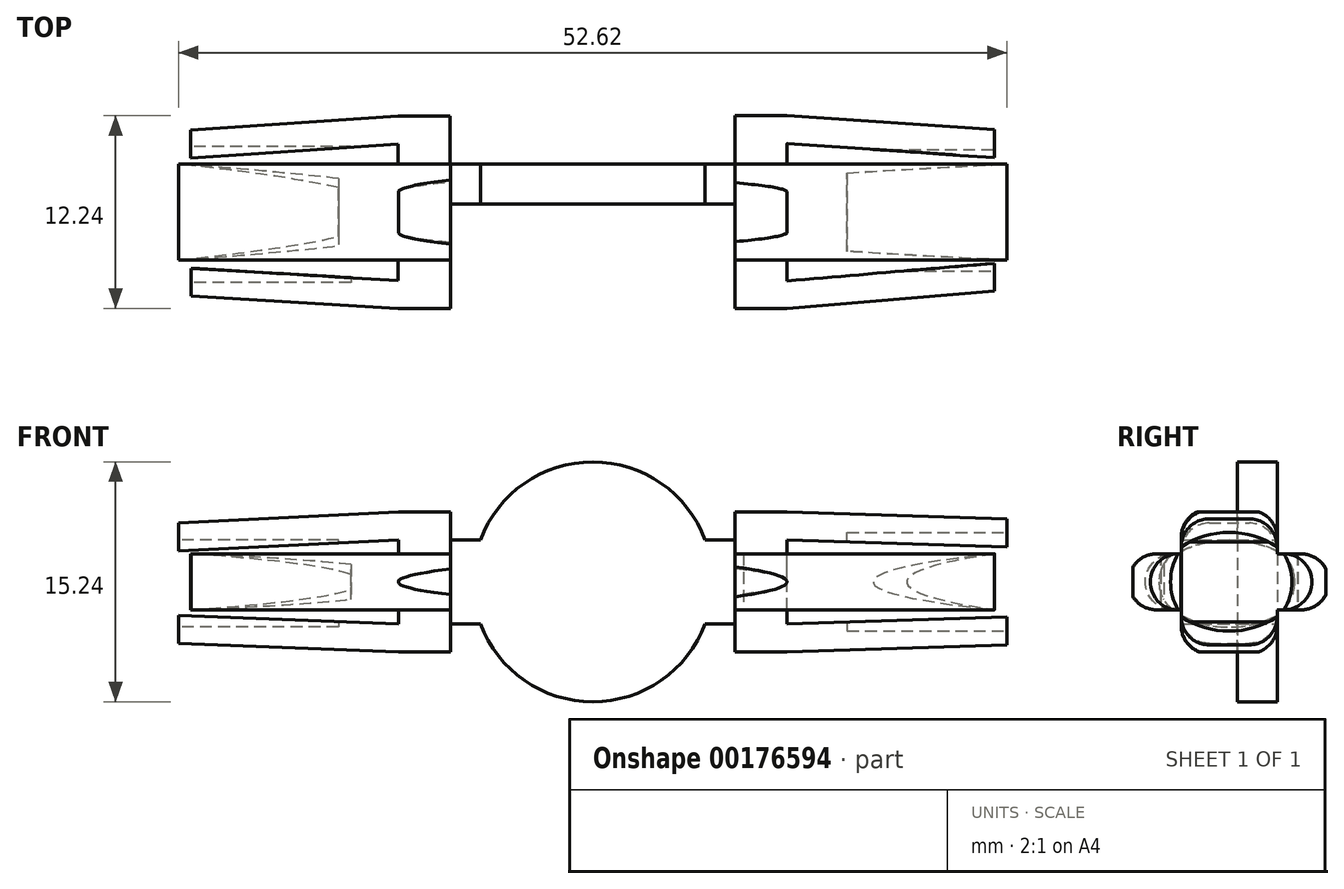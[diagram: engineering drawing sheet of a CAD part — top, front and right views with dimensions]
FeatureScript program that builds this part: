
annotation { "Feature Type Name" : "Feature", "Feature Type Description" : "" }
export const myFeature = defineFeature(function(context is Context, id is Id, definition is map)
    precondition{}
    {
        {
            var Q0;
            Q0=qCreatedBy(makeId("Front.planeOp"),FACE);
            var sketch = newSketch(context, id + "F0", { "sketchPlane" : qUnion([Q0])});
            skArc(sketch, "E0", {"start": v(7.14, 2.67) * mm, "mid": v(0, 7.62) * mm, "end": v(-7.14, 2.67) * mm});
            skLineSegment(sketch, "E1", {"start": v(-7.14, 2.67) * mm, "end": v(-9.04, 2.67) * mm});
            skLineSegment(sketch, "E2", {"start": v(-7.14, -2.67) * mm, "end": v(-9.04, -2.67) * mm});
            skLineSegment(sketch, "E3", {"start": v(-9.04, -2.67) * mm, "end": v(-9.04, 2.67) * mm});
            skLineSegment(sketch, "E4", {"start": v(7.14, 2.67) * mm, "end": v(9.04, 2.67) * mm});
            skLineSegment(sketch, "E5", {"start": v(7.14, -2.67) * mm, "end": v(9.04, -2.67) * mm});
            skLineSegment(sketch, "E6", {"start": v(9.04, -2.67) * mm, "end": v(9.04, 2.67) * mm});
            skArc(sketch, "E7.trimOffspring", {"start": v(-7.14, -2.67) * mm, "mid": v(0, -7.62) * mm, "end": v(7.14, -2.67) * mm});
            skLineSegment(sketch, "E8", {"start": v(-12.35, -2.67) * mm, "end": v(-12.35, 2.67) * mm});
            skLineSegment(sketch, "E9", {"start": v(-9.04, -2.67) * mm, "end": v(-9.04, -4.45) * mm});
            skLineSegment(sketch, "E10", {"start": v(-9.04, -4.45) * mm, "end": v(-12.35, -4.45) * mm});
            skLineSegment(sketch, "E11", {"start": v(-12.35, -4.45) * mm, "end": v(-26.3, -3.9) * mm});
            skLineSegment(sketch, "E12", {"start": v(-26.3, -3.9) * mm, "end": v(-26.3, -2.13) * mm});
            skLineSegment(sketch, "E13", {"start": v(-26.3, -2.13) * mm, "end": v(-12.35, -2.67) * mm});
            skLineSegment(sketch, "E14", {"start": v(-9.04, 2.67) * mm, "end": v(-9.04, 4.45) * mm});
            skLineSegment(sketch, "E15", {"start": v(-9.04, 4.45) * mm, "end": v(-12.35, 4.45) * mm});
            skLineSegment(sketch, "E16", {"start": v(-12.35, 4.45) * mm, "end": v(-26.3, 3.73) * mm});
            skLineSegment(sketch, "E17", {"start": v(-26.3, 3.73) * mm, "end": v(-26.3, 1.95) * mm});
            skLineSegment(sketch, "E18", {"start": v(-26.3, 1.95) * mm, "end": v(-12.35, 2.67) * mm});
            skLineSegment(sketch, "E19", {"start": v(9.04, 2.67) * mm, "end": v(9.04, 4.44) * mm});
            skLineSegment(sketch, "E20", {"start": v(9.04, 4.44) * mm, "end": v(12.35, 4.44) * mm});
            skLineSegment(sketch, "E21", {"start": v(9.04, -2.67) * mm, "end": v(9.04, -4.44) * mm});
            skLineSegment(sketch, "E22", {"start": v(9.04, -4.44) * mm, "end": v(12.35, -4.44) * mm});
            skLineSegment(sketch, "E23", {"start": v(12.35, -2.67) * mm, "end": v(12.35, 2.67) * mm});
            skLineSegment(sketch, "E24", {"start": v(12.35, -4.44) * mm, "end": v(26.3, -4) * mm});
            skLineSegment(sketch, "E25", {"start": v(26.3, -4) * mm, "end": v(26.3, -2.23) * mm});
            skLineSegment(sketch, "E26", {"start": v(26.3, -2.23) * mm, "end": v(12.35, -2.67) * mm});
            skLineSegment(sketch, "E27", {"start": v(12.35, 4.44) * mm, "end": v(26.3, 4) * mm});
            skLineSegment(sketch, "E28", {"start": v(26.3, 4) * mm, "end": v(26.3, 2.23) * mm});
            skLineSegment(sketch, "E29", {"start": v(26.3, 2.23) * mm, "end": v(12.35, 2.67) * mm});
            skLineSegment(sketch, "E30", {"start": v(12.35, 4.44) * mm, "end": v(12.35, 2.67) * mm});
            skLineSegment(sketch, "E31", {"start": v(12.35, -4.44) * mm, "end": v(12.35, -2.67) * mm});
            skSolve(sketch);
        }
        {
            var Q0;
            Q0 = qSketchRegion(id + "F0", true);
            extrude(context, id + "F1", {"entities" : qUnion([Q0]), "depth" : 6.1 * mm});
        }
        {
            var Q0;
            Q0=makeQuery(id+"F1.opExtrude","CAP_FACE",FACE,{"disambiguationData":[OSD([sQuery(id+"F0.wireOp",EDGE,"E0"),sQuery(id+"F0.wireOp",EDGE,"E1"),sQuery(id+"F0.wireOp",EDGE,"E2"),sQuery(id+"F0.wireOp",EDGE,"E4"),sQuery(id+"F0.wireOp",EDGE,"E5"),sQuery(id+"F0.wireOp",EDGE,"E7.trimOffspring"),sQuery(id+"F0.wireOp",EDGE,"E8"),sQuery(id+"F0.wireOp",EDGE,"E9"),sQuery(id+"F0.wireOp",EDGE,"E10"),sQuery(id+"F0.wireOp",EDGE,"E11"),sQuery(id+"F0.wireOp",EDGE,"E12"),sQuery(id+"F0.wireOp",EDGE,"E13"),sQuery(id+"F0.wireOp",EDGE,"E14"),sQuery(id+"F0.wireOp",EDGE,"E15"),sQuery(id+"F0.wireOp",EDGE,"E16"),sQuery(id+"F0.wireOp",EDGE,"E17"),sQuery(id+"F0.wireOp",EDGE,"E18"),sQuery(id+"F0.wireOp",EDGE,"E19"),sQuery(id+"F0.wireOp",EDGE,"E20"),sQuery(id+"F0.wireOp",EDGE,"E21"),sQuery(id+"F0.wireOp",EDGE,"E22"),sQuery(id+"F0.wireOp",EDGE,"E23"),sQuery(id+"F0.wireOp",EDGE,"E24"),sQuery(id+"F0.wireOp",EDGE,"E25"),sQuery(id+"F0.wireOp",EDGE,"E26"),sQuery(id+"F0.wireOp",EDGE,"E27"),sQuery(id+"F0.wireOp",EDGE,"E28"),sQuery(id+"F0.wireOp",EDGE,"E29")])],"isStart":false});
            var sketch = newSketch(context, id + "F2", { "sketchPlane" : qUnion([Q0])});
            skLineSegment(sketch, "E32", {"start": v(-9.04, 2.67) * mm, "end": v(-9.04, -2.67) * mm});
            skLineSegment(sketch, "E33", {"start": v(9.04, 2.67) * mm, "end": v(9.04, -2.67) * mm});
            skSolve(sketch);
        }
        {
            var Q0;
            Q0 = qSketchRegion(id + "F2", true);
            var Q1;
            Q1=makeQuery(id+"F2.imprint","IMPRINT",FACE,{"disambiguationData":[TD([[makeQuery(id+"F2.imprint","IMPRINT",EDGE,{"derivedFrom":sQuery(id+"F2.wireOp",EDGE,"E32")}),1.0]])]});
            extrude(context, id + "F3", {"entities" : qUnion([Q0, Q1]), "operationType" : NewBodyOperationType.REMOVE, "oppositeDirection" : true, "depth" : 3.56 * mm});
        }
        {
            var Q0;
            Q0=qCreatedBy(makeId("Top.planeOp"),FACE);
            var sketch = newSketch(context, id + "F4", { "sketchPlane" : qUnion([Q0])});
            skLineSegment(sketch, "E34", {"start": v(-9.05, 0) * mm, "end": v(-9.05, 3.06) * mm});
            skLineSegment(sketch, "E35", {"start": v(-12.36, 3.06) * mm, "end": v(-9.05, 3.06) * mm});
            skPoint(sketch, "E36.start.orphan", {"position": v(-12.36, 0) * mm});
            skLineSegment(sketch, "E37", {"start": v(-12.36, 3.06) * mm, "end": v(-25.54, 2.17) * mm});
            skLineSegment(sketch, "E38", {"start": v(-25.54, 2.17) * mm, "end": v(-25.54, 0.4) * mm});
            skLineSegment(sketch, "E39", {"start": v(-12.36, 1.27) * mm, "end": v(-25.54, 0.4) * mm});
            skLineSegment(sketch, "E40", {"start": v(-12.36, 1.27) * mm, "end": v(-12.36, 0) * mm});
            skLineSegment(sketch, "E41", {"start": v(-12.36, 0) * mm, "end": v(-9.05, 0) * mm});
            skSolve(sketch);
        }
        {
            var Q0;
            Q0 = qSketchRegion(id + "F4", true);
            extrude(context, id + "F5", {"entities" : qUnion([Q0]), "operationType" : NewBodyOperationType.ADD, "depth" : 1.78 * mm});
        }
        {
            var Q0;
            Q0=makeQuery(id+"F5.opExtrude","CAP_FACE",FACE,{"disambiguationData":[OSD([sQuery(id+"F4.wireOp",EDGE,"E34"),sQuery(id+"F4.wireOp",EDGE,"E35"),sQuery(id+"F4.wireOp",EDGE,"E37"),sQuery(id+"F4.wireOp",EDGE,"E38"),sQuery(id+"F4.wireOp",EDGE,"E39"),sQuery(id+"F4.wireOp",EDGE,"E40"),sQuery(id+"F4.wireOp",EDGE,"E41")])],"isStart":true});
            extrude(context, id + "F6", {"entities" : qUnion([Q0]), "operationType" : NewBodyOperationType.ADD, "depth" : 1.78 * mm});
        }
        {
            var Q0;
            Q0=qCreatedBy(makeId("Top.planeOp"),FACE);
            var sketch = newSketch(context, id + "F7", { "sketchPlane" : qUnion([Q0])});
            skLineSegment(sketch, "E42", {"start": v(-9.04, -6.1) * mm, "end": v(-9.04, -9.16) * mm});
            skLineSegment(sketch, "E43", {"start": v(-9.04, -9.16) * mm, "end": v(-12.35, -9.16) * mm});
            skLineSegment(sketch, "E44", {"start": v(-12.35, -7.39) * mm, "end": v(-12.35, -6.1) * mm});
            skLineSegment(sketch, "E45", {"start": v(-12.35, -6.1) * mm, "end": v(-9.04, -6.1) * mm});
            skLineSegment(sketch, "E46", {"start": v(-12.35, -9.16) * mm, "end": v(-25.52, -8.38) * mm});
            skLineSegment(sketch, "E47", {"start": v(-25.52, -8.38) * mm, "end": v(-25.52, -6.61) * mm});
            skLineSegment(sketch, "E48", {"start": v(-12.35, -7.39) * mm, "end": v(-25.52, -6.61) * mm});
            skSolve(sketch);
        }
        {
            var Q0;
            Q0=makeQuery(id+"F7.imprint","IMPRINT",FACE,{"disambiguationData":[TD([[makeQuery(id+"F7.imprint","IMPRINT",EDGE,{"derivedFrom":sQuery(id+"F7.wireOp",EDGE,"E42")}),-1.0]])]});
            extrude(context, id + "F8", {"entities" : qUnion([Q0]), "operationType" : NewBodyOperationType.ADD, "depth" : 1.78 * mm});
        }
        {
            var Q0;
            Q0=makeQuery(id+"F8.opExtrude","CAP_FACE",FACE,{"disambiguationData":[OSD([sQuery(id+"F7.wireOp",EDGE,"E42"),sQuery(id+"F7.wireOp",EDGE,"E43"),sQuery(id+"F7.wireOp",EDGE,"E44"),sQuery(id+"F7.wireOp",EDGE,"E45"),sQuery(id+"F7.wireOp",EDGE,"E46"),sQuery(id+"F7.wireOp",EDGE,"E47"),sQuery(id+"F7.wireOp",EDGE,"E48")])],"isStart":true});
            extrude(context, id + "F9", {"entities" : qUnion([Q0]), "operationType" : NewBodyOperationType.ADD, "depth" : 1.78 * mm});
        }
        {
            var Q0;
            {var subQ0=sQuery(id+"F7.wireOp",EDGE,"E47");Q0=makeQuery(id+"F9.boolean.opBoolean","MERGE",FACE,{"derivedFrom":[makeQuery(id+"F8.opExtrude","SWEPT_FACE",FACE,{"disambiguationData":[OSD([subQ0])]}),makeQuery(id+"F9.opExtrude","SWEPT_FACE",FACE,{"disambiguationData":[OSD([subQ0])]})]});}
            var sketch = newSketch(context, id + "F10", { "sketchPlane" : qUnion([Q0])});
            skArc(sketch, "E49", {"start": v(6.61, -1.78) * mm, "mid": v(7.5, 0) * mm, "end": v(6.61, 1.78) * mm});
            skLineSegment(sketch, "E50", {"start": v(6.61, 1.78) * mm, "end": v(6.61, -1.78) * mm});
            skSolve(sketch);
        }
        {
            var Q0;
            Q0 = qSketchRegion(id + "F10", true);
            extrude(context, id + "F11", {"entities" : qUnion([Q0]), "operationType" : NewBodyOperationType.REMOVE, "oppositeDirection" : true, "depth" : 10.16 * mm});
        }
        {
            var Q0;
            Q0=makeQuery(id+"F1.opExtrude","SWEPT_FACE",FACE,{"disambiguationData":[OSD([sQuery(id+"F0.wireOp",EDGE,"E17")])]});
            var sketch = newSketch(context, id + "F12", { "sketchPlane" : qUnion([Q0])});
            skArc(sketch, "E51", {"start": v(6.1, 1.95) * mm, "mid": v(3.05, 2.65) * mm, "end": v(0, 1.95) * mm});
            skLineSegment(sketch, "E52", {"start": v(6.1, 1.95) * mm, "end": v(0, 1.95) * mm});
            skSolve(sketch);
        }
        {
            var Q0;
            Q0 = qSketchRegion(id + "F12", true);
            extrude(context, id + "F13", {"entities" : qUnion([Q0]), "operationType" : NewBodyOperationType.REMOVE, "oppositeDirection" : true, "depth" : 10.16 * mm});
        }
        {
            var Q0;
            Q0=makeQuery(id+"F1.opExtrude","SWEPT_FACE",FACE,{"disambiguationData":[OSD([sQuery(id+"F0.wireOp",EDGE,"E12")])]});
            var sketch = newSketch(context, id + "F14", { "sketchPlane" : qUnion([Q0])});
            skArc(sketch, "E53", {"start": v(0, -2.13) * mm, "mid": v(3.05, -2.88) * mm, "end": v(6.1, -2.13) * mm});
            skLineSegment(sketch, "E54", {"start": v(6.1, -2.13) * mm, "end": v(0, -2.13) * mm});
            skSolve(sketch);
        }
        {
            var Q0;
            Q0 = qSketchRegion(id + "F14", true);
            extrude(context, id + "F15", {"entities" : qUnion([Q0]), "operationType" : NewBodyOperationType.REMOVE, "oppositeDirection" : true, "depth" : 10.16 * mm});
        }
        {
            var Q0;
            {var subQ0=sQuery(id+"F4.wireOp",EDGE,"E38");Q0=makeQuery(id+"F6.boolean.opBoolean","MERGE",FACE,{"derivedFrom":[makeQuery(id+"F5.opExtrude","SWEPT_FACE",FACE,{"disambiguationData":[OSD([subQ0])]}),makeQuery(id+"F6.opExtrude","SWEPT_FACE",FACE,{"disambiguationData":[OSD([subQ0])]})]});}
            var sketch = newSketch(context, id + "F16", { "sketchPlane" : qUnion([Q0])});
            skArc(sketch, "E55", {"start": v(-0.4, 1.78) * mm, "mid": v(-1.12, 0) * mm, "end": v(-0.4, -1.78) * mm});
            skLineSegment(sketch, "E56", {"start": v(-0.4, 1.78) * mm, "end": v(-0.4, -1.78) * mm});
            skSolve(sketch);
        }
        {
            var Q0;
            Q0 = qSketchRegion(id + "F16", true);
            extrude(context, id + "F17", {"entities" : qUnion([Q0]), "operationType" : NewBodyOperationType.REMOVE, "oppositeDirection" : true, "depth" : 10.16 * mm});
        }
        {
            var Q0;
            Q0=qCreatedBy(makeId("Top.planeOp"),FACE);
            var sketch = newSketch(context, id + "F18", { "sketchPlane" : qUnion([Q0])});
            skLineSegment(sketch, "E57", {"start": v(9.04, 0) * mm, "end": v(9.04, 3.08) * mm});
            skLineSegment(sketch, "E58", {"start": v(9.04, 3.08) * mm, "end": v(12.34, 3.08) * mm});
            skLineSegment(sketch, "E59", {"start": v(12.34, 0) * mm, "end": v(9.04, 0) * mm});
            skLineSegment(sketch, "E60", {"start": v(12.34, 3.08) * mm, "end": v(25.52, 2.2) * mm});
            skLineSegment(sketch, "E61", {"start": v(25.52, 2.2) * mm, "end": v(25.52, 0.41) * mm});
            skLineSegment(sketch, "E62", {"start": v(25.52, 0.41) * mm, "end": v(12.34, 1.31) * mm});
            skLineSegment(sketch, "E63.trimOffspring", {"start": v(12.34, 1.31) * mm, "end": v(12.34, 0) * mm});
            skSolve(sketch);
        }
        {
            var Q0;
            Q0 = qSketchRegion(id + "F18", true);
            extrude(context, id + "F19", {"entities" : qUnion([Q0]), "operationType" : NewBodyOperationType.ADD, "depth" : 1.78 * mm});
        }
        {
            var Q0;
            Q0=qCreatedBy(makeId("Top.planeOp"),FACE);
            var sketch = newSketch(context, id + "F20", { "sketchPlane" : qUnion([Q0])});
            skLineSegment(sketch, "E64", {"start": v(9.04, -6.1) * mm, "end": v(9.04, -9.16) * mm});
            skLineSegment(sketch, "E65", {"start": v(9.04, -9.16) * mm, "end": v(12.33, -9.16) * mm});
            skLineSegment(sketch, "E66", {"start": v(12.33, -7.41) * mm, "end": v(12.33, -6.1) * mm});
            skLineSegment(sketch, "E67", {"start": v(12.33, -6.1) * mm, "end": v(9.04, -6.1) * mm});
            skLineSegment(sketch, "E68", {"start": v(12.33, -9.16) * mm, "end": v(25.5, -8.07) * mm});
            skLineSegment(sketch, "E69", {"start": v(25.5, -8.07) * mm, "end": v(25.5, -6.3) * mm});
            skLineSegment(sketch, "E70", {"start": v(25.5, -6.3) * mm, "end": v(12.33, -7.41) * mm});
            skSolve(sketch);
        }
        {
            var Q0;
            Q0 = qSketchRegion(id + "F20", true);
            extrude(context, id + "F21", {"entities" : qUnion([Q0]), "operationType" : NewBodyOperationType.ADD, "depth" : 1.78 * mm});
        }
        {
            var Q0;
            Q0=makeQuery(id+"F21.opExtrude","CAP_FACE",FACE,{"disambiguationData":[OSD([sQuery(id+"F20.wireOp",EDGE,"E64"),sQuery(id+"F20.wireOp",EDGE,"E65"),sQuery(id+"F20.wireOp",EDGE,"E66"),sQuery(id+"F20.wireOp",EDGE,"E67"),sQuery(id+"F20.wireOp",EDGE,"E68"),sQuery(id+"F20.wireOp",EDGE,"E69"),sQuery(id+"F20.wireOp",EDGE,"E70")])],"isStart":true});
            extrude(context, id + "F22", {"entities" : qUnion([Q0]), "operationType" : NewBodyOperationType.ADD, "depth" : 1.78 * mm});
        }
        {
            var Q0;
            Q0=makeQuery(id+"F19.opExtrude","CAP_FACE",FACE,{"disambiguationData":[OSD([sQuery(id+"F18.wireOp",EDGE,"E57"),sQuery(id+"F18.wireOp",EDGE,"E58"),sQuery(id+"F18.wireOp",EDGE,"E59"),sQuery(id+"F18.wireOp",EDGE,"E60"),sQuery(id+"F18.wireOp",EDGE,"E61"),sQuery(id+"F18.wireOp",EDGE,"E62"),sQuery(id+"F18.wireOp",EDGE,"E63.trimOffspring")])],"isStart":true});
            extrude(context, id + "F23", {"entities" : qUnion([Q0]), "operationType" : NewBodyOperationType.ADD, "depth" : 1.78 * mm});
        }
        {
            var Q0;
            {var subQ0=sQuery(id+"F20.wireOp",EDGE,"E69");Q0=makeQuery(id+"F22.boolean.opBoolean","MERGE",FACE,{"derivedFrom":[makeQuery(id+"F21.opExtrude","SWEPT_FACE",FACE,{"disambiguationData":[OSD([subQ0])]}),makeQuery(id+"F22.opExtrude","SWEPT_FACE",FACE,{"disambiguationData":[OSD([subQ0])]})]});}
            var sketch = newSketch(context, id + "F24", { "sketchPlane" : qUnion([Q0])});
            skArc(sketch, "E71", {"start": v(-6.3, 1.78) * mm, "mid": v(-6.77, 0) * mm, "end": v(-6.3, -1.78) * mm});
            skLineSegment(sketch, "E72", {"start": v(-6.3, -1.78) * mm, "end": v(-6.3, 1.78) * mm});
            skSolve(sketch);
        }
        {
            var Q0;
            Q0=makeQuery(id+"F1.opExtrude","SWEPT_FACE",FACE,{"disambiguationData":[OSD([sQuery(id+"F0.wireOp",EDGE,"E25")])]});
            var sketch = newSketch(context, id + "F25", { "sketchPlane" : qUnion([Q0])});
            skArc(sketch, "E73", {"start": v(-6.1, -2.23) * mm, "mid": v(-3.05, -3.13) * mm, "end": v(0, -2.23) * mm});
            skLineSegment(sketch, "E74", {"start": v(-6.1, -2.23) * mm, "end": v(0, -2.23) * mm});
            skSolve(sketch);
        }
        {
            var Q0;
            {var subQ0=sQuery(id+"F18.wireOp",EDGE,"E61");Q0=makeQuery(id+"F23.boolean.opBoolean","MERGE",FACE,{"derivedFrom":[makeQuery(id+"F19.opExtrude","SWEPT_FACE",FACE,{"disambiguationData":[OSD([subQ0])]}),makeQuery(id+"F23.opExtrude","SWEPT_FACE",FACE,{"disambiguationData":[OSD([subQ0])]})]});}
            var sketch = newSketch(context, id + "F26", { "sketchPlane" : qUnion([Q0])});
            skArc(sketch, "E75", {"start": v(0.41, -1.78) * mm, "mid": v(0.94, 0) * mm, "end": v(0.41, 1.78) * mm});
            skLineSegment(sketch, "E76", {"start": v(0.41, -1.78) * mm, "end": v(0.41, 1.78) * mm});
            skSolve(sketch);
        }
        {
            var Q0;
            Q0=makeQuery(id+"F1.opExtrude","SWEPT_FACE",FACE,{"disambiguationData":[OSD([sQuery(id+"F0.wireOp",EDGE,"E28")])]});
            var sketch = newSketch(context, id + "F27", { "sketchPlane" : qUnion([Q0])});
            skArc(sketch, "E77", {"start": v(0, 2.23) * mm, "mid": v(-3.05, 3.14) * mm, "end": v(-6.1, 2.23) * mm});
            skLineSegment(sketch, "E78", {"start": v(-6.1, 2.23) * mm, "end": v(0, 2.23) * mm});
            skSolve(sketch);
        }
        {
            var Q0;
            Q0=makeQuery(id+"F24.imprint","IMPRINT",FACE,{"disambiguationData":[TD([[makeQuery(id+"F24.imprint","IMPRINT",EDGE,{"derivedFrom":sQuery(id+"F24.wireOp",EDGE,"E71")}),1.0]])]});
            var Q1;
            Q1=makeQuery(id+"F27.imprint","IMPRINT",FACE,{"disambiguationData":[TD([[makeQuery(id+"F27.imprint","IMPRINT",EDGE,{"derivedFrom":sQuery(id+"F27.wireOp",EDGE,"E77")}),1.0]])]});
            var Q2;
            Q2=makeQuery(id+"F26.imprint","IMPRINT",FACE,{"disambiguationData":[TD([[makeQuery(id+"F26.imprint","IMPRINT",EDGE,{"derivedFrom":sQuery(id+"F26.wireOp",EDGE,"E75")}),1.0]])]});
            var Q3;
            Q3=makeQuery(id+"F25.imprint","IMPRINT",FACE,{"disambiguationData":[TD([[makeQuery(id+"F25.imprint","IMPRINT",EDGE,{"derivedFrom":sQuery(id+"F25.wireOp",EDGE,"E73")}),1.0]])]});
            extrude(context, id + "F28", {"entities" : qUnion([Q0, Q1, Q2, Q3]), "operationType" : NewBodyOperationType.REMOVE, "oppositeDirection" : true, "depth" : 10.16 * mm});
        }
        {
            var Q0;
            Q0=makeQuery(id+"F22.opExtrude","CAP_EDGE",EDGE,{"disambiguationData":[OSD([sQuery(id+"F20.wireOp",EDGE,"E68")])],"isStart":false});
            var Q1;
            Q1=makeQuery(id+"F21.opExtrude","CAP_EDGE",EDGE,{"disambiguationData":[OSD([sQuery(id+"F20.wireOp",EDGE,"E68")])],"isStart":false});
            var Q2;
            Q2=makeQuery(id+"F1.opExtrude","CAP_EDGE",EDGE,{"disambiguationData":[OSD([sQuery(id+"F0.wireOp",EDGE,"E24")])],"isStart":false});
            var Q3;
            Q3=makeQuery(id+"F1.opExtrude","CAP_EDGE",EDGE,{"disambiguationData":[OSD([sQuery(id+"F0.wireOp",EDGE,"E24")])],"isStart":true});
            var Q4;
            Q4=makeQuery(id+"F1.opExtrude","CAP_EDGE",EDGE,{"disambiguationData":[OSD([sQuery(id+"F0.wireOp",EDGE,"E27")])],"isStart":false});
            var Q5;
            Q5=makeQuery(id+"F1.opExtrude","CAP_EDGE",EDGE,{"disambiguationData":[OSD([sQuery(id+"F0.wireOp",EDGE,"E27")])],"isStart":true});
            var Q6;
            Q6=makeQuery(id+"F23.opExtrude","CAP_EDGE",EDGE,{"disambiguationData":[OSD([sQuery(id+"F18.wireOp",EDGE,"E60")])],"isStart":false});
            var Q7;
            Q7=makeQuery(id+"F19.opExtrude","CAP_EDGE",EDGE,{"disambiguationData":[OSD([sQuery(id+"F18.wireOp",EDGE,"E60")])],"isStart":false});
            fillet(context, id + "F29", {"entities" : qUnion([Q0, Q1, Q2, Q3, Q4, Q5, Q6, Q7]), "radius" : 1.78 * mm, "tangentPropagation" : true, "allowEdgeOverflow" : false});
        }
        {
            var Q0;
            Q0=makeQuery(id+"F8.opExtrude","CAP_EDGE",EDGE,{"disambiguationData":[OSD([sQuery(id+"F7.wireOp",EDGE,"E46")])],"isStart":false});
            var Q1;
            Q1=makeQuery(id+"F9.opExtrude","CAP_EDGE",EDGE,{"disambiguationData":[OSD([sQuery(id+"F7.wireOp",EDGE,"E46")])],"isStart":false});
            var Q2;
            Q2=makeQuery(id+"F1.opExtrude","CAP_EDGE",EDGE,{"disambiguationData":[OSD([sQuery(id+"F0.wireOp",EDGE,"E16")])],"isStart":false});
            var Q3;
            Q3=makeQuery(id+"F1.opExtrude","CAP_EDGE",EDGE,{"disambiguationData":[OSD([sQuery(id+"F0.wireOp",EDGE,"E16")])],"isStart":true});
            var Q4;
            Q4=makeQuery(id+"F1.opExtrude","CAP_EDGE",EDGE,{"disambiguationData":[OSD([sQuery(id+"F0.wireOp",EDGE,"E11")])],"isStart":false});
            var Q5;
            Q5=makeQuery(id+"F5.opExtrude","CAP_EDGE",EDGE,{"disambiguationData":[OSD([sQuery(id+"F4.wireOp",EDGE,"E37")])],"isStart":false});
            var Q6;
            Q6=makeQuery(id+"F1.opExtrude","CAP_EDGE",EDGE,{"disambiguationData":[OSD([sQuery(id+"F0.wireOp",EDGE,"E11")])],"isStart":true});
            var Q7;
            Q7=makeQuery(id+"F6.opExtrude","CAP_EDGE",EDGE,{"disambiguationData":[OSD([sQuery(id+"F4.wireOp",EDGE,"E37")])],"isStart":false});
            fillet(context, id + "F30", {"entities" : qUnion([Q0, Q1, Q2, Q3, Q4, Q5, Q6, Q7]), "radius" : 1.78 * mm, "tangentPropagation" : true, "allowEdgeOverflow" : false});
        }
    });
